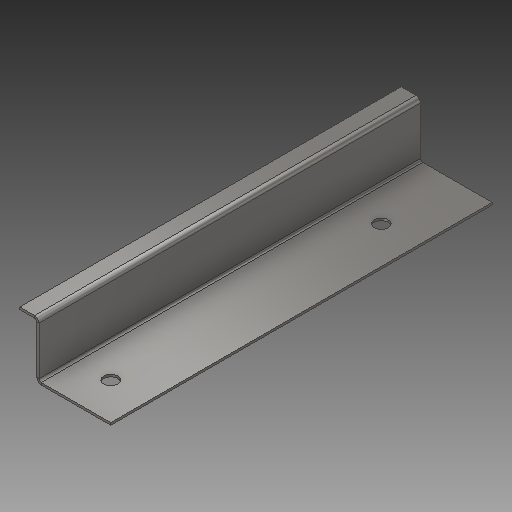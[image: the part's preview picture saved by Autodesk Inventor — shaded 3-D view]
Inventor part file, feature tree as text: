
AUTODESK INVENTOR PART (.ipt)
format: ipt  version: 2017 (Build 210142000, 142)  size: 178,176 bytes
history: native  units: mm
features: sheet_metal_op x3, sketch x2, other x2, extrude x1
ambient origin geometry x8: Origin, YZ Plane, XZ Plane, XY Plane, X Axis, Y Axis, Z Axis, Center Point
bodies: Solid1 (feature_tree)
feature tree (8):
  sheet_metal_op  "Contour Flange1"
  extrude  "Extrusion1"  Depth=37.0mm
  sketch  "Sketch1"  dims[d0=50.0mm d1=37.0mm]
  other  "Plate1"
  sheet_metal_op  "Bend1"
  sheet_metal_op  "Corner1"
  sketch  "Sketch2"  dims[d2=11.5mm d3=1.5mm d4=0.75mm d5=3.0mm d6=1.5mm d7=258.0mm d8=1.5mm d9=0.5mm d10=6.0mm d11=1.5mm d12=1.5mm d13=9.525mm d14=9.525mm d15=25.0mm d16=25.0mm d17=25.0mm d18=50.0mm d19=10.0mm d20=0.0mm]
  other  "Definition1"
